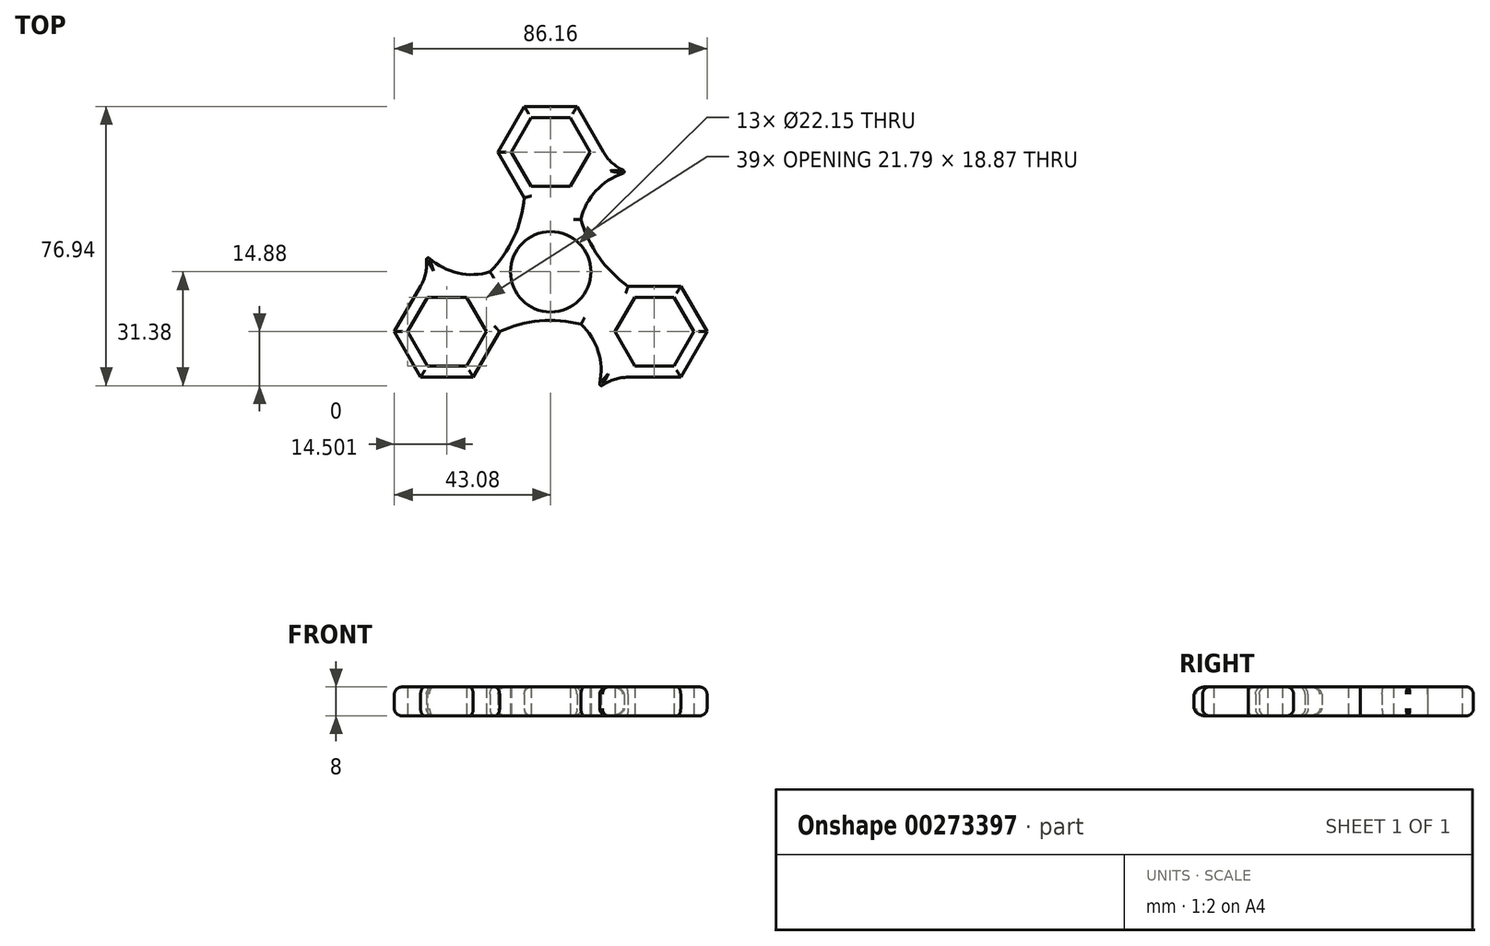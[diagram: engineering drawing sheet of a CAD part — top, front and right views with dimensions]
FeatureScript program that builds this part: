
annotation { "Feature Type Name" : "Feature", "Feature Type Description" : "" }
export const myFeature = defineFeature(function(context is Context, id is Id, definition is map)
    precondition{}
    {
        {
            var Q0;
            Q0=qCreatedBy(makeId("Top.planeOp"),FACE);
            var sketch = newSketch(context, id + "F0", { "sketchPlane" : qUnion([Q0])});
            skCircle(sketch, "E0", {"center": v(0, 0) * mm, "radius": 11.07 * mm});
            skPoint(sketch, "E1.0.midPoint", {"position": v(0, 23.37) * mm});
            skLineSegment(sketch, "E2.1", {"start": v(-7.25, 20.44) * mm, "end": v(-14.5, 33) * mm});
            skLineSegment(sketch, "E2.2", {"start": v(-14.5, 33) * mm, "end": v(-7.25, 45.56) * mm});
            skLineSegment(sketch, "E2.3", {"start": v(-7.25, 45.56) * mm, "end": v(7.25, 45.56) * mm});
            skLineSegment(sketch, "E2.4", {"start": v(7.25, 45.56) * mm, "end": v(14.5, 33) * mm});
            skPoint(sketch, "E2.0.midPoint", {"position": v(0, 20.44) * mm});
            skLineSegment(sketch, "E3.1.7", {"start": v(-14.08, -16.5) * mm, "end": v(-21.33, -29.06) * mm});
            skLineSegment(sketch, "E3.1.8", {"start": v(-21.33, -29.06) * mm, "end": v(-35.83, -29.06) * mm});
            skLineSegment(sketch, "E3.1.9", {"start": v(-35.83, -29.06) * mm, "end": v(-43.08, -16.5) * mm});
            skLineSegment(sketch, "E3.1.10", {"start": v(-43.08, -16.5) * mm, "end": v(-35.83, -3.94) * mm});
            skPoint(sketch, "E3.1.12", {"position": v(-17.7, -10.22) * mm});
            skPoint(sketch, "E3.1.13", {"position": v(-20.24, -11.68) * mm});
            skLineSegment(sketch, "E3.2.7", {"start": v(21.33, -3.94) * mm, "end": v(35.83, -3.94) * mm});
            skLineSegment(sketch, "E3.2.8", {"start": v(35.83, -3.94) * mm, "end": v(43.08, -16.5) * mm});
            skLineSegment(sketch, "E3.2.9", {"start": v(43.08, -16.5) * mm, "end": v(35.83, -29.06) * mm});
            skLineSegment(sketch, "E3.2.10", {"start": v(35.83, -29.06) * mm, "end": v(21.33, -29.06) * mm});
            skPoint(sketch, "E3.2.12", {"position": v(17.7, -10.22) * mm});
            skPoint(sketch, "E3.2.13", {"position": v(28.58, -16.5) * mm});
            skArc(sketch, "E4", {"start": v(-21.33, -3.94) * mm, "mid": v(-11.61, 6.7) * mm, "end": v(-7.25, 20.44) * mm});
            skArc(sketch, "E5.1.0", {"start": v(14.08, -16.5) * mm, "mid": v(0, -13.4) * mm, "end": v(-14.08, -16.5) * mm});
            skArc(sketch, "E5.2.0", {"start": v(7.25, 20.44) * mm, "mid": v(11.61, 6.7) * mm, "end": v(21.33, -3.94) * mm});
            skArc(sketch, "E6", {"start": v(14.5, 33) * mm, "mid": v(17.4, 29.6) * mm, "end": v(21.33, 27.46) * mm});
            skArc(sketch, "E7.1.1", {"start": v(-35.83, -3.94) * mm, "mid": v(-34.33, 0.27) * mm, "end": v(-34.45, 4.74) * mm});
            skArc(sketch, "E7.2.1", {"start": v(21.33, -29.06) * mm, "mid": v(16.93, -29.87) * mm, "end": v(13.12, -32.2) * mm});
            skArc(sketch, "E8", {"start": v(-34.45, 4.74) * mm, "mid": v(-26.26, -0.2) * mm, "end": v(-16.7, 0) * mm});
            skArc(sketch, "E9.1.0", {"start": v(13.12, -32.2) * mm, "mid": v(13.3, -22.64) * mm, "end": v(8.35, -14.46) * mm});
            skArc(sketch, "E9.2.0", {"start": v(21.33, 27.46) * mm, "mid": v(12.96, 22.84) * mm, "end": v(8.35, 14.46) * mm});
            skLineSegment(sketch, "E10", {"start": v(0, 0) * mm, "end": v(0, 33) * mm, "construction": true});
            skCircle(sketch, "E11.cCircle", {"center": v(0, 33) * mm, "radius": 9.44 * mm, "construction": true});
            skLineSegment(sketch, "E11.0", {"start": v(5.45, 23.56) * mm, "end": v(-5.45, 23.56) * mm});
            skLineSegment(sketch, "E11.1", {"start": v(-5.45, 23.56) * mm, "end": v(-10.9, 33) * mm});
            skLineSegment(sketch, "E11.2", {"start": v(-10.9, 33) * mm, "end": v(-5.45, 42.44) * mm});
            skLineSegment(sketch, "E11.3", {"start": v(-5.45, 42.44) * mm, "end": v(5.45, 42.44) * mm});
            skLineSegment(sketch, "E11.4", {"start": v(5.45, 42.44) * mm, "end": v(10.9, 33) * mm});
            skLineSegment(sketch, "E11.5", {"start": v(10.9, 33) * mm, "end": v(5.45, 23.56) * mm});
            skPoint(sketch, "E11.0.midPoint", {"position": v(0, 23.56) * mm});
            skCircle(sketch, "E12.1.0", {"center": v(-28.58, -16.5) * mm, "radius": 9.44 * mm, "construction": true});
            skLineSegment(sketch, "E12.1.1", {"start": v(-23.13, -25.93) * mm, "end": v(-34.03, -25.93) * mm});
            skLineSegment(sketch, "E12.1.2", {"start": v(-17.68, -16.5) * mm, "end": v(-23.13, -25.93) * mm});
            skLineSegment(sketch, "E12.1.3", {"start": v(-23.13, -7.06) * mm, "end": v(-17.68, -16.5) * mm});
            skLineSegment(sketch, "E12.1.4", {"start": v(-34.03, -7.06) * mm, "end": v(-23.13, -7.06) * mm});
            skLineSegment(sketch, "E12.1.5", {"start": v(-39.47, -16.5) * mm, "end": v(-34.03, -7.06) * mm});
            skLineSegment(sketch, "E12.1.6", {"start": v(-34.03, -25.93) * mm, "end": v(-39.47, -16.5) * mm});
            skCircle(sketch, "E12.2.0", {"center": v(28.58, -16.5) * mm, "radius": 9.44 * mm, "construction": true});
            skLineSegment(sketch, "E12.2.1", {"start": v(34.03, -7.06) * mm, "end": v(39.47, -16.5) * mm});
            skLineSegment(sketch, "E12.2.2", {"start": v(23.13, -7.06) * mm, "end": v(34.03, -7.06) * mm});
            skLineSegment(sketch, "E12.2.3", {"start": v(17.68, -16.5) * mm, "end": v(23.13, -7.06) * mm});
            skLineSegment(sketch, "E12.2.4", {"start": v(23.13, -25.93) * mm, "end": v(17.68, -16.5) * mm});
            skLineSegment(sketch, "E12.2.5", {"start": v(34.03, -25.93) * mm, "end": v(23.13, -25.94) * mm});
            skLineSegment(sketch, "E12.2.6", {"start": v(39.47, -16.5) * mm, "end": v(34.03, -25.93) * mm});
            skSolve(sketch);
        }
        {
            var Q0;
            Q0=makeQuery(id+"F0.imprint","IMPRINT",FACE,{"disambiguationData":[TD([[makeQuery(id+"F0.imprint","IMPRINT",EDGE,{"derivedFrom":sQuery(id+"F0.wireOp",EDGE,"E0")}),-1.0]])]});
            extrude(context, id + "F1", {"entities" : qUnion([Q0]), "depth" : 8 * mm});
        }
        {
            var Q0;
            Q0=makeQuery(id+"F1.opExtrude","CAP_EDGE",EDGE,{"disambiguationData":[OSD([sQuery(id+"F0.wireOp",EDGE,"E4")])],"isStart":false});
            var Q1;
            Q1=makeQuery(id+"F1.opExtrude","CAP_EDGE",EDGE,{"disambiguationData":[OSD([sQuery(id+"F0.wireOp",EDGE,"E3.1.9")])],"isStart":false});
            var Q2;
            Q2=makeQuery(id+"F1.opExtrude","CAP_EDGE",EDGE,{"disambiguationData":[OSD([sQuery(id+"F0.wireOp",EDGE,"E5.1.0")])],"isStart":false});
            var Q3;
            Q3=makeQuery(id+"F1.opExtrude","CAP_EDGE",EDGE,{"disambiguationData":[OSD([sQuery(id+"F0.wireOp",EDGE,"E5.2.0")])],"isStart":false});
            var Q4;
            Q4=makeQuery(id+"F1.opExtrude","CAP_EDGE",EDGE,{"disambiguationData":[OSD([sQuery(id+"F0.wireOp",EDGE,"E2.3")])],"isStart":false});
            var Q5;
            Q5=makeQuery(id+"F1.opExtrude","CAP_EDGE",EDGE,{"disambiguationData":[OSD([sQuery(id+"F0.wireOp",EDGE,"E3.2.9")])],"isStart":false});
            var Q6;
            Q6=makeQuery(id+"F1.opExtrude","CAP_EDGE",EDGE,{"disambiguationData":[OSD([sQuery(id+"F0.wireOp",EDGE,"E2.2")])],"isStart":false});
            var Q7;
            Q7=makeQuery(id+"F1.opExtrude","CAP_EDGE",EDGE,{"disambiguationData":[OSD([sQuery(id+"F0.wireOp",EDGE,"E2.1")])],"isStart":false});
            var Q8;
            Q8=makeQuery(id+"F1.opExtrude","CAP_EDGE",EDGE,{"disambiguationData":[OSD([sQuery(id+"F0.wireOp",EDGE,"E2.4")])],"isStart":false});
            var Q9;
            Q9=makeQuery(id+"F1.opExtrude","CAP_EDGE",EDGE,{"disambiguationData":[OSD([sQuery(id+"F0.wireOp",EDGE,"27lDcBJv-5MQt-QsWd-Lt6n-5IwVHu0BAJwC")])],"isStart":false});
            var Q10;
            Q10=makeQuery(id+"F1.opExtrude","CAP_EDGE",EDGE,{"disambiguationData":[OSD([sQuery(id+"F0.wireOp",EDGE,"E3.2.7")])],"isStart":false});
            var Q11;
            Q11=makeQuery(id+"F1.opExtrude","CAP_EDGE",EDGE,{"disambiguationData":[OSD([sQuery(id+"F0.wireOp",EDGE,"E3.2.8")])],"isStart":false});
            var Q12;
            Q12=makeQuery(id+"F1.opExtrude","CAP_EDGE",EDGE,{"disambiguationData":[OSD([sQuery(id+"F0.wireOp",EDGE,"E3.2.10")])],"isStart":false});
            var Q13;
            Q13=makeQuery(id+"F1.opExtrude","CAP_EDGE",EDGE,{"disambiguationData":[OSD([sQuery(id+"F0.wireOp",EDGE,"E7.2.1")])],"isStart":false});
            var Q14;
            Q14=makeQuery(id+"F1.opExtrude","CAP_EDGE",EDGE,{"disambiguationData":[OSD([sQuery(id+"F0.wireOp",EDGE,"E7.2.0")])],"isStart":false});
            var Q15;
            Q15=makeQuery(id+"F1.opExtrude","CAP_EDGE",EDGE,{"disambiguationData":[OSD([sQuery(id+"F0.wireOp",EDGE,"E3.1.7")])],"isStart":false});
            var Q16;
            Q16=makeQuery(id+"F1.opExtrude","CAP_EDGE",EDGE,{"disambiguationData":[OSD([sQuery(id+"F0.wireOp",EDGE,"E3.1.8")])],"isStart":false});
            var Q17;
            Q17=makeQuery(id+"F1.opExtrude","CAP_EDGE",EDGE,{"disambiguationData":[OSD([sQuery(id+"F0.wireOp",EDGE,"E3.1.10")])],"isStart":false});
            var Q18;
            Q18=makeQuery(id+"F1.opExtrude","CAP_EDGE",EDGE,{"disambiguationData":[OSD([sQuery(id+"F0.wireOp",EDGE,"E7.1.0")])],"isStart":false});
            var Q19;
            Q19=makeQuery(id+"F1.opExtrude","CAP_EDGE",EDGE,{"disambiguationData":[OSD([sQuery(id+"F0.wireOp",EDGE,"E5.2.0")])],"isStart":true});
            var Q20;
            Q20=makeQuery(id+"F1.opExtrude","CAP_EDGE",EDGE,{"disambiguationData":[OSD([sQuery(id+"F0.wireOp",EDGE,"27lDcBJv-5MQt-QsWd-Lt6n-5IwVHu0BAJwC")])],"isStart":true});
            var Q21;
            Q21=makeQuery(id+"F1.opExtrude","CAP_EDGE",EDGE,{"disambiguationData":[OSD([sQuery(id+"F0.wireOp",EDGE,"E6")])],"isStart":true});
            var Q22;
            Q22=makeQuery(id+"F1.opExtrude","CAP_EDGE",EDGE,{"disambiguationData":[OSD([sQuery(id+"F0.wireOp",EDGE,"E2.4")])],"isStart":true});
            var Q23;
            Q23=makeQuery(id+"F1.opExtrude","CAP_EDGE",EDGE,{"disambiguationData":[OSD([sQuery(id+"F0.wireOp",EDGE,"E2.3")])],"isStart":true});
            var Q24;
            Q24=makeQuery(id+"F1.opExtrude","CAP_EDGE",EDGE,{"disambiguationData":[OSD([sQuery(id+"F0.wireOp",EDGE,"E2.2")])],"isStart":true});
            var Q25;
            Q25=makeQuery(id+"F1.opExtrude","CAP_EDGE",EDGE,{"disambiguationData":[OSD([sQuery(id+"F0.wireOp",EDGE,"E2.1")])],"isStart":true});
            var Q26;
            Q26=makeQuery(id+"F1.opExtrude","CAP_EDGE",EDGE,{"disambiguationData":[OSD([sQuery(id+"F0.wireOp",EDGE,"E4")])],"isStart":true});
            var Q27;
            Q27=makeQuery(id+"F1.opExtrude","CAP_EDGE",EDGE,{"disambiguationData":[OSD([sQuery(id+"F0.wireOp",EDGE,"E7.1.0")])],"isStart":true});
            var Q28;
            Q28=makeQuery(id+"F1.opExtrude","CAP_EDGE",EDGE,{"disambiguationData":[OSD([sQuery(id+"F0.wireOp",EDGE,"E7.1.1")])],"isStart":true});
            var Q29;
            Q29=makeQuery(id+"F1.opExtrude","CAP_EDGE",EDGE,{"disambiguationData":[OSD([sQuery(id+"F0.wireOp",EDGE,"E3.1.10")])],"isStart":true});
            var Q30;
            Q30=makeQuery(id+"F1.opExtrude","CAP_EDGE",EDGE,{"disambiguationData":[OSD([sQuery(id+"F0.wireOp",EDGE,"E3.1.7")])],"isStart":true});
            var Q31;
            Q31=makeQuery(id+"F1.opExtrude","CAP_EDGE",EDGE,{"disambiguationData":[OSD([sQuery(id+"F0.wireOp",EDGE,"E5.1.0")])],"isStart":true});
            var Q32;
            Q32=makeQuery(id+"F1.opExtrude","CAP_EDGE",EDGE,{"disambiguationData":[OSD([sQuery(id+"F0.wireOp",EDGE,"E7.2.1")])],"isStart":true});
            var Q33;
            Q33=makeQuery(id+"F1.opExtrude","CAP_EDGE",EDGE,{"disambiguationData":[OSD([sQuery(id+"F0.wireOp",EDGE,"E3.2.10")])],"isStart":true});
            var Q34;
            Q34=makeQuery(id+"F1.opExtrude","CAP_EDGE",EDGE,{"disambiguationData":[OSD([sQuery(id+"F0.wireOp",EDGE,"E3.2.9")])],"isStart":true});
            var Q35;
            Q35=makeQuery(id+"F1.opExtrude","CAP_EDGE",EDGE,{"disambiguationData":[OSD([sQuery(id+"F0.wireOp",EDGE,"E3.2.8")])],"isStart":true});
            var Q36;
            Q36=makeQuery(id+"F1.opExtrude","CAP_EDGE",EDGE,{"disambiguationData":[OSD([sQuery(id+"F0.wireOp",EDGE,"E3.2.7")])],"isStart":true});
            var Q37;
            Q37=makeQuery(id+"F1.opExtrude","CAP_EDGE",EDGE,{"disambiguationData":[OSD([sQuery(id+"F0.wireOp",EDGE,"E3.1.9")])],"isStart":true});
            var Q38;
            Q38=makeQuery(id+"F1.opExtrude","CAP_EDGE",EDGE,{"disambiguationData":[OSD([sQuery(id+"F0.wireOp",EDGE,"E3.1.8")])],"isStart":true});
            var Q39;
            Q39=makeQuery(id+"F1.opExtrude","CAP_EDGE",EDGE,{"disambiguationData":[OSD([sQuery(id+"F0.wireOp",EDGE,"E7.2.0")])],"isStart":true});
            var Q40;
            Q40=makeQuery(id+"F1.opExtrude","CAP_EDGE",EDGE,{"disambiguationData":[OSD([sQuery(id+"F0.wireOp",EDGE,"E8")])],"isStart":true});
            var Q41;
            Q41=makeQuery(id+"F1.opExtrude","CAP_EDGE",EDGE,{"disambiguationData":[OSD([sQuery(id+"F0.wireOp",EDGE,"E8")])],"isStart":false});
            var Q42;
            Q42=makeQuery(id+"F1.opExtrude","CAP_EDGE",EDGE,{"disambiguationData":[OSD([sQuery(id+"F0.wireOp",EDGE,"E9.1.0")])],"isStart":true});
            var Q43;
            Q43=makeQuery(id+"F1.opExtrude","CAP_EDGE",EDGE,{"disambiguationData":[OSD([sQuery(id+"F0.wireOp",EDGE,"E9.2.0")])],"isStart":true});
            var Q44;
            Q44=makeQuery(id+"F1.opExtrude","CAP_EDGE",EDGE,{"disambiguationData":[OSD([sQuery(id+"F0.wireOp",EDGE,"E9.2.0")])],"isStart":false});
            var Q45;
            Q45=makeQuery(id+"F1.opExtrude","CAP_EDGE",EDGE,{"disambiguationData":[OSD([sQuery(id+"F0.wireOp",EDGE,"E9.1.0")])],"isStart":false});
            fillet(context, id + "F2", {"entities" : qUnion([Q0, Q1, Q2, Q3, Q4, Q5, Q6, Q7, Q8, Q9, Q10, Q11, Q12, Q13, Q14, Q15, Q16, Q17, Q18, Q19, Q20, Q21, Q22, Q23, Q24, Q25, Q26, Q27, Q28, Q29, Q30, Q31, Q32, Q33, Q34, Q35, Q36, Q37, Q38, Q39, Q40, Q41, Q42, Q43, Q44, Q45]), "radius" : 2 * mm, "tangentPropagation" : true, "allowEdgeOverflow" : false});
        }
        {
            var Q0;
            Q0=makeQuery(id+"F1.opExtrude","SWEPT_EDGE",EDGE,{"disambiguationData":[OSD([sQuery(id+"F0.wireOp",EDGE,"E7.1.0"),sQuery(id+"F0.wireOp",EDGE,"E7.1.1")])]});
            var Q1;
            Q1=makeQuery(id+"F1.opExtrude","SWEPT_EDGE",EDGE,{"disambiguationData":[OSD([sQuery(id+"F0.wireOp",EDGE,"E7.2.0"),sQuery(id+"F0.wireOp",EDGE,"E7.2.1")])]});
            var Q2;
            Q2=makeQuery(id+"F1.opExtrude","SWEPT_EDGE",EDGE,{"disambiguationData":[OSD([sQuery(id+"F0.wireOp",EDGE,"E6"),sQuery(id+"F0.wireOp",EDGE,"27lDcBJv-5MQt-QsWd-Lt6n-5IwVHu0BAJwC")])]});
            fillet(context, id + "F3", {"entities" : qUnion([Q0, Q1, Q2]), "radius" : .5 * mm, "tangentPropagation" : true, "allowEdgeOverflow" : false});
        }
    });
